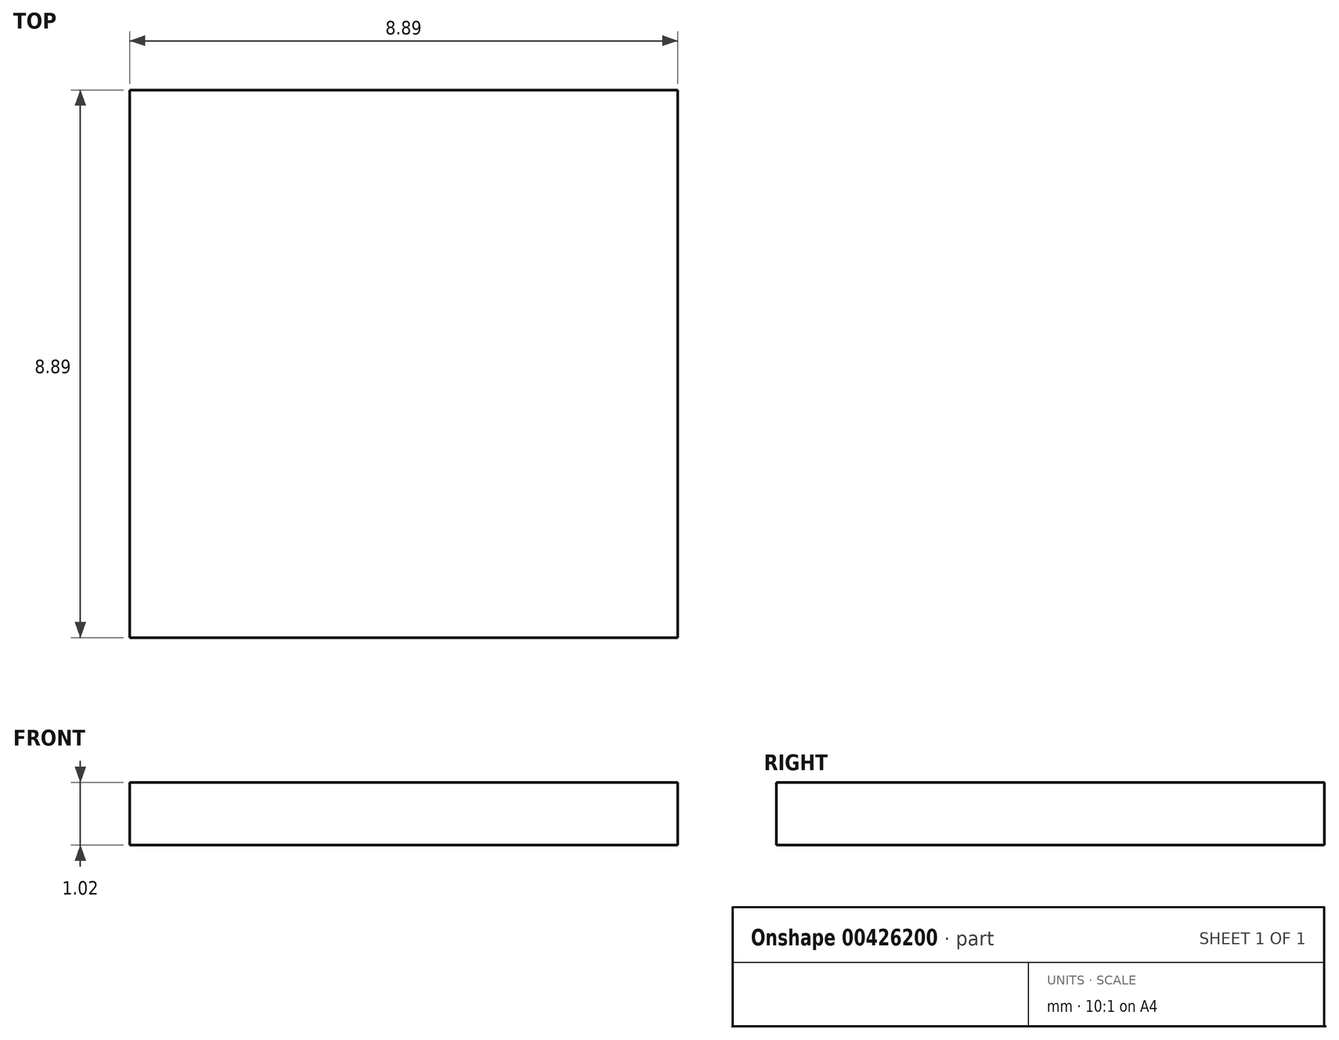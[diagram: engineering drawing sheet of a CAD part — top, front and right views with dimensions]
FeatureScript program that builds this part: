
annotation { "Feature Type Name" : "Feature", "Feature Type Description" : "" }
export const myFeature = defineFeature(function(context is Context, id is Id, definition is map)
    precondition{}
    {
        {
            var Q0;
            Q0=qCreatedBy(makeId("Top.planeOp"),FACE);
            var sketch = newSketch(context, id + "F0", { "sketchPlane" : qUnion([Q0])});
            skLineSegment(sketch, "E0.bottom", {"start": v(0, 0) * mm, "end": v(8.89, 0) * mm});
            skLineSegment(sketch, "E0.top", {"start": v(0, 8.9) * mm, "end": v(8.89, 8.9) * mm});
            skLineSegment(sketch, "E0.left", {"start": v(0, 0) * mm, "end": v(0, 8.89) * mm});
            skLineSegment(sketch, "E0.right", {"start": v(8.9, 0) * mm, "end": v(8.9, 8.89) * mm});
            skSolve(sketch);
        }
        {
            var Q0;
            Q0 = qSketchRegion(id + "F0", true);
            extrude(context, id + "F1", {"entities" : qUnion([Q0]), "depth" : 1.02 * mm});
        }
    });
